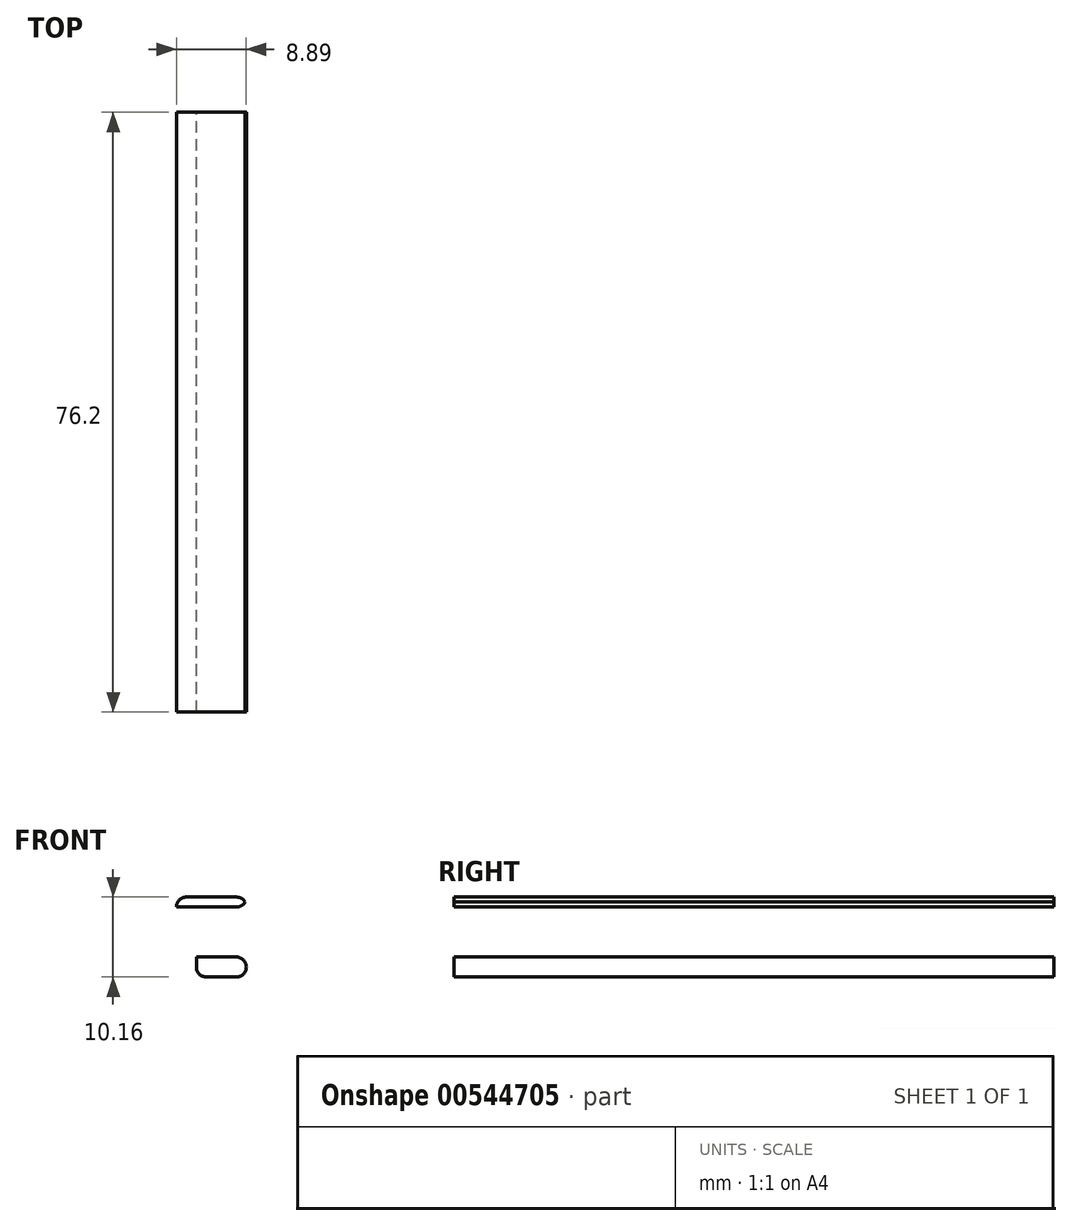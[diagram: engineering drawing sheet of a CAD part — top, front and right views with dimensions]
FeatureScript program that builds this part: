
annotation { "Feature Type Name" : "Feature", "Feature Type Description" : "" }
export const myFeature = defineFeature(function(context is Context, id is Id, definition is map)
    precondition{}
    {
        {
            var Q0;
            Q0=qCreatedBy(makeId("Front.planeOp"),FACE);
            var sketch = newSketch(context, id + "F0", { "sketchPlane" : qUnion([Q0])});
            skLineSegment(sketch, "E0.bottom", {"start": v(-40.57, 26.6) * mm, "end": v(-34.22, 26.6) * mm});
            skLineSegment(sketch, "E0.top", {"start": v(-40.57, 20.25) * mm, "end": v(-34.22, 20.25) * mm});
            skLineSegment(sketch, "E0.left", {"start": v(-40.57, 26.6) * mm, "end": v(-40.57, 20.25) * mm});
            skLineSegment(sketch, "E0.right", {"start": v(-34.22, 26.6) * mm, "end": v(-34.22, 20.25) * mm});
            skLineSegment(sketch, "E1.bottom", {"start": v(-34.22, 26.6) * mm, "end": v(-43.1, 26.6) * mm});
            skLineSegment(sketch, "E1.top", {"start": v(-34.22, 27.87) * mm, "end": v(-43.1, 27.87) * mm});
            skLineSegment(sketch, "E1.left", {"start": v(-34.22, 26.6) * mm, "end": v(-34.22, 27.87) * mm});
            skLineSegment(sketch, "E1.right", {"start": v(-43.1, 26.6) * mm, "end": v(-43.1, 27.87) * mm});
            skLineSegment(sketch, "E2.bottom", {"start": v(-43.1, 26.6) * mm, "end": v(-40.57, 26.6) * mm});
            skLineSegment(sketch, "E2.top", {"start": v(-43.1, 17.7) * mm, "end": v(-40.57, 17.7) * mm});
            skLineSegment(sketch, "E2.left", {"start": v(-43.1, 26.6) * mm, "end": v(-43.1, 17.7) * mm});
            skLineSegment(sketch, "E2.right", {"start": v(-40.57, 26.6) * mm, "end": v(-40.57, 17.7) * mm});
            skLineSegment(sketch, "E3.bottom", {"start": v(-40.57, 17.7) * mm, "end": v(-34.22, 17.7) * mm});
            skLineSegment(sketch, "E3.left", {"start": v(-40.57, 17.7) * mm, "end": v(-40.57, 20.25) * mm});
            skLineSegment(sketch, "E3.right", {"start": v(-34.22, 17.7) * mm, "end": v(-34.22, 20.25) * mm});
            skSolve(sketch);
        }
        {
            var Q0;
            Q0=makeQuery(id+"F0.imprint","IMPRINT",FACE,{"disambiguationData":[TD([[makeQuery(id+"F0.imprint","IMPRINT",EDGE,{"derivedFrom":sQuery(id+"F0.wireOp",EDGE,"E3.bottom")}),1.0]])]});
            var Q1;
            Q1=makeQuery(id+"F0.imprint","IMPRINT",FACE,{"disambiguationData":[TD([[makeQuery(id+"F0.imprint","IMPRINT",EDGE,{"derivedFrom":sQuery(id+"F0.wireOp",EDGE,"E2.bottom")}),-1.0]])]});
            var Q2;
            Q2=makeQuery(id+"F0.imprint","IMPRINT",FACE,{"disambiguationData":[TD([[makeQuery(id+"F0.imprint","IMPRINT",EDGE,{"derivedFrom":sQuery(id+"F0.wireOp",EDGE,"E1.bottom")}),-1.0]])]});
            extrude(context, id + "F1", {"entities" : qUnion([Q0, Q1, Q2]), "depth" : 76.2 * mm, "offsetDistance" : 25.4 * mm});
        }
        {
            var Q0;
            Q0=makeQuery(id+"F1.opExtrude","SWEPT_EDGE",EDGE,{"disambiguationData":[OSD([sQuery(id+"F0.wireOp",EDGE,"E1.top"),sQuery(id+"F0.wireOp",EDGE,"E1.right")])]});
            fillet(context, id + "F2", {"entities" : qUnion([Q0]), "radius" : 1.27 * mm, "tangentPropagation" : true, "allowEdgeOverflow" : false});
        }
        {
            var Q0;
            Q0=makeQuery(id+"F1.opExtrude","SWEPT_EDGE",EDGE,{"disambiguationData":[OSD([sQuery(id+"F0.wireOp",EDGE,"E2.top"),sQuery(id+"F0.wireOp",EDGE,"E2.left")])]});
            var Q1;
            Q1=makeQuery(id+"F1.opExtrude","SWEPT_EDGE",EDGE,{"disambiguationData":[OSD([sQuery(id+"F0.wireOp",EDGE,"E0.right"),sQuery(id+"F0.wireOp",EDGE,"E1.bottom"),sQuery(id+"F0.wireOp",EDGE,"E1.left")])]});
            var Q2;
            Q2=makeQuery(id+"F1.opExtrude","SWEPT_EDGE",EDGE,{"disambiguationData":[OSD([sQuery(id+"F0.wireOp",EDGE,"E0.right"),sQuery(id+"F0.wireOp",EDGE,"E0.top"),sQuery(id+"F0.wireOp",EDGE,"E3.right")])]});
            var Q3;
            Q3=makeQuery(id+"F1.opExtrude","SWEPT_EDGE",EDGE,{"disambiguationData":[OSD([sQuery(id+"F0.wireOp",EDGE,"E3.bottom"),sQuery(id+"F0.wireOp",EDGE,"E3.right")])]});
            var Q4;
            Q4=makeQuery(id+"F1.opExtrude","SWEPT_EDGE",EDGE,{"disambiguationData":[OSD([sQuery(id+"F0.wireOp",EDGE,"E1.top"),sQuery(id+"F0.wireOp",EDGE,"E1.left")])]});
            fillet(context, id + "F3", {"entities" : qUnion([Q0, Q1, Q2, Q3, Q4]), "radius" : 1.27 * mm, "tangentPropagation" : true, "allowEdgeOverflow" : false});
        }
    });
